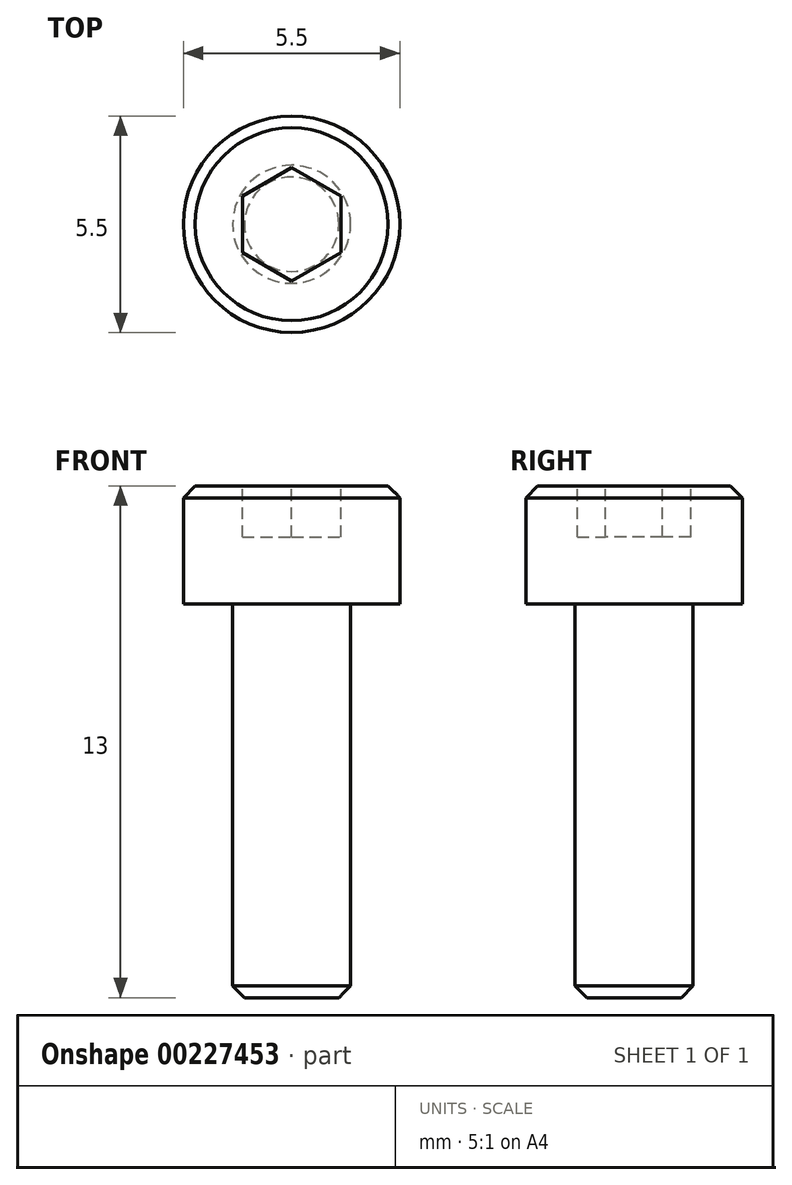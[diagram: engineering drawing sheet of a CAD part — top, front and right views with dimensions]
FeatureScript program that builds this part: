
annotation { "Feature Type Name" : "Feature", "Feature Type Description" : "" }
export const myFeature = defineFeature(function(context is Context, id is Id, definition is map)
    precondition{}
    {
        {
            assignVariable(context, id + "F0", {"name" : "M", "anyValue" : 3});
        }
        {
            assignVariable(context, id + "F1", {"name" : "length", "anyValue" : 10});
        }
        {
            var Q0;
            Q0=qCreatedBy(makeId("Top.planeOp"),FACE);
            var sketch = newSketch(context, id + "F2", { "sketchPlane" : qUnion([Q0])});
            skCircle(sketch, "E0", {"center": v(0, 0) * mm, "radius": 1.5 * mm});
            skCircle(sketch, "E1", {"center": v(0, 0) * mm, "radius": 2.75 * mm});
            skSolve(sketch);
        }
        {
            var Q0;
            Q0=makeQuery(id+"F2.imprint","IMPRINT",FACE,{"disambiguationData":[TD([[makeQuery(id+"F2.imprint","IMPRINT",EDGE,{"derivedFrom":sQuery(id+"F2.wireOp",EDGE,"E0")}),1.0]])]});
            extrude(context, id + "F3", {"entities" : qUnion([Q0]), "oppositeDirection" : true, "depth" : getVariable(context, 'length') * mm});
        }
        {
            var Q0;
            Q0=qSketchRegion(id+"F2",true);
            var Q1;
            Q1=makeQuery(id+"F3.opExtrude","CAP_FACE",FACE,{"disambiguationData":[OSD([sQuery(id+"F2.wireOp",EDGE,"E0")])],"isStart":true});
            extrude(context, id + "F4", {"entities" : qUnion([Q0, Q1]), "operationType" : NewBodyOperationType.ADD, "depth" : (getVariable(context, 'M')) * mm});
        }
        {
            var Q0;
            Q0=makeQuery(id+"F3.opExtrude","CAP_EDGE",EDGE,{"disambiguationData":[OSD([sQuery(id+"F2.wireOp",EDGE,"E0")])],"isStart":false});
            var Q1;
            Q1=makeQuery(id+"F4.opExtrude","CAP_EDGE",EDGE,{"disambiguationData":[OSD([sQuery(id+"F2.wireOp",EDGE,"E1")])],"isStart":false});
            var Q2;
            Q2=makeQuery(id+"FbGFCUzPbhfoxTw_1.opExtrude","CAP_EDGE",EDGE,{"disambiguationData":[OSD([sQuery(id+"FgaPx5IOfmBmuk3_1.wireOp",EDGE,"RfBxyrST-LDbJ-RpBC-vAS8-07GQ8Ko211GC")])],"isStart":false});
            chamfer(context, id + "F5", {"entities" : qUnion([Q0, Q1, Q2]), "width" : 0.3 * mm, "tangentPropagation" : true});
        }
        {
            var Q0;
            {var subQ0=sQuery(id+"F2.wireOp",EDGE,"E0");Q0=makeQuery(id+"F4.boolean.opBoolean","MERGE",FACE,{"derivedFrom":[makeQuery(id+"F4.opExtrude","CAP_FACE",FACE,{"disambiguationData":[OSD([subQ0,sQuery(id+"F2.wireOp",EDGE,"E1")])],"isStart":false}),makeQuery(id+"F4.opExtrude","CAP_FACE",FACE,{"disambiguationData":[OSD([subQ0])],"isStart":false})]});}
            var sketch = newSketch(context, id + "F6", { "sketchPlane" : qUnion([Q0])});
            skCircle(sketch, "E2.cCircle", {"center": v(0, 0) * mm, "radius": 1.25 * mm, "construction": true});
            skLineSegment(sketch, "E2.0", {"start": v(1.25, 0.72) * mm, "end": v(1.25, -0.72) * mm});
            skLineSegment(sketch, "E2.1", {"start": v(1.25, -0.72) * mm, "end": v(0, -1.44) * mm});
            skLineSegment(sketch, "E2.2", {"start": v(0, -1.44) * mm, "end": v(-1.25, -0.72) * mm});
            skLineSegment(sketch, "E2.3", {"start": v(-1.25, -0.72) * mm, "end": v(-1.25, 0.72) * mm});
            skLineSegment(sketch, "E2.4", {"start": v(-1.25, 0.72) * mm, "end": v(0, 1.44) * mm});
            skLineSegment(sketch, "E2.5", {"start": v(0, 1.44) * mm, "end": v(1.25, 0.72) * mm});
            skPoint(sketch, "E2.0.midPoint", {"position": v(1.25, 0) * mm});
            skSolve(sketch);
        }
        {
            var Q0;
            Q0=makeQuery(id+"F6.imprint","IMPRINT",FACE,{"disambiguationData":[TD([[makeQuery(id+"F6.imprint","IMPRINT",EDGE,{"derivedFrom":sQuery(id+"F6.wireOp",EDGE,"E2.0")}),-1.0]])]});
            extrude(context, id + "F7", {"entities" : qUnion([Q0]), "operationType" : NewBodyOperationType.REMOVE, "oppositeDirection" : true, "depth" : 1.3 * mm});
        }
    });
